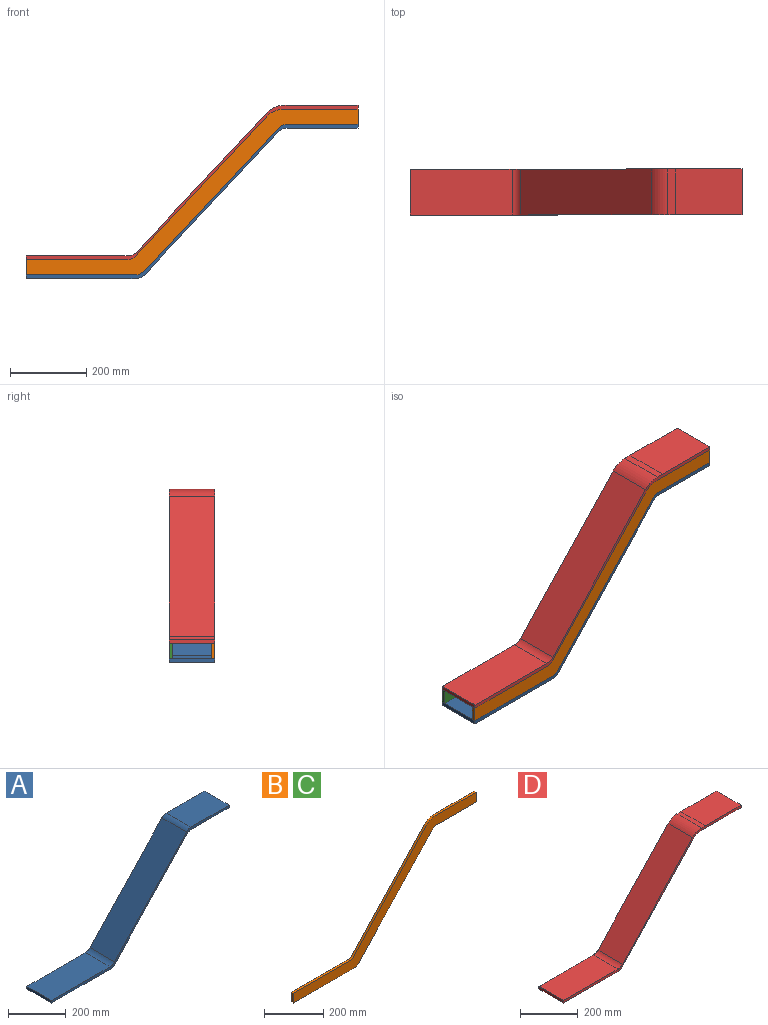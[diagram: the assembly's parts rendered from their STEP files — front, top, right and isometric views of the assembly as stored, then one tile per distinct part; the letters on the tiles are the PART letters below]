
ASSEMBLY  parts=4 mates=5
PART A: 15 faces, bbox 869.5x120x403.8 mm
  f0: cylinder r=30mm len=120mm, axis (0,1,0), area 2942mm2, adj f1,f12,f13,f14
  f1: plane 185.87x120mm, normal (0,0,-1), area 22305mm2, adj f0,f2,f13,f14
  f2: plane 120x9.99mm, normal (1,0,0), area 1198.4mm2, adj f1,f3,f13,f14
  f3: plane 187.01x120mm, normal (0,0,1), area 22441.2mm2, adj f2,f4,f13,f14
  f4: cylinder r=30mm len=120mm, axis (0,1,0), area 2942mm2, adj f3,f5,f13,f14
  f5: plane 374.85x351.71mm, normal (-0.73,0,0.68), area 61682.5mm2, adj f4,f6,f13,f14
  f6: cylinder r=30mm len=120mm, axis (0,1,0), area 2942mm2, adj f5,f7,f13,f14
  f7: plane 287.01x120mm, normal (0,0,1), area 34441.2mm2, adj f6,f8,f13,f14
  f8: plane 120x10mm, normal (-1,0,0), area 1200mm2, adj f7,f9,f13,f14
  f9: plane 120x1.14mm, normal (0.01,0,-1), area 136.3mm2, adj f8,f10,f13,f14
  f10: plane 287.01x120mm, normal (0,0,-1), area 34441.2mm2, adj f9,f11,f13,f14
  f11: cylinder r=30mm len=120mm, axis (0,1,0), area 2942mm2, adj f10,f12,f13,f14
  f12: plane 374.85x351.71mm, normal (0.73,0,-0.68), area 61682.5mm2, adj f0,f11,f13,f14
  f13: plane 869.49x403.8mm, normal (0,-1,0), area 9130.4mm2, adj f0,f1,f2,f3,f4,f5,f6,f7
  f14: plane 869.49x403.8mm, normal (0,1,0), area 9130.4mm2, adj f0,f1,f2,f3,f4,f5,f6,f7
PART B: 14 faces, bbox 869.5x9x433.8 mm
  f0: plane 40x9mm, normal (1,0,0), area 360mm2, adj f1,f11,f12,f13
  f1: plane 194.64x9mm, normal (0,0,1), area 1751.7mm2, adj f0,f2,f12,f13
  f2: cylinder r=60mm len=43.76mm, axis (0,1,0), area 441.3mm2, adj f1,f3,f12,f13
  f3: plane 365.38x342.83mm, normal (-0.73,0,0.68), area 4509.3mm2, adj f2,f4,f12,f13
  f4: cylinder r=30mm len=21.88mm, axis (0,1,0), area 220.7mm2, adj f3,f5,f12,f13
  f5: plane 266.39x9mm, normal (0,0,1), area 2397.6mm2, adj f4,f6,f12,f13
  f6: plane 40x9mm, normal (-1,0,0), area 360mm2, adj f5,f7,f12,f13
  f7: plane 287.01x9mm, normal (0,0,-1), area 2583.1mm2, adj f6,f8,f12,f13
  f8: cylinder r=30mm len=21.88mm, axis (0,1,0), area 220.7mm2, adj f7,f9,f12,f13
  f9: plane 374.85x351.71mm, normal (0.73,0,-0.68), area 4626.2mm2, adj f8,f10,f12,f13
  f10: cylinder r=30mm len=21.88mm, axis (0,1,0), area 220.7mm2, adj f9,f11,f12,f13
  f11: plane 187.01x9mm, normal (0,0,-1), area 1683.1mm2, adj f0,f10,f12,f13
  f12: plane 869.49x433.8mm, normal (0,-1,0), area 42832.1mm2, adj f0,f1,f2,f3,f4,f5,f6,f7
  f13: plane 869.49x433.8mm, normal (0,1,0), area 42832.1mm2, adj f0,f1,f2,f3,f4,f5,f6,f7
PART C: same geometry as B
PART D: 16 faces, bbox 869.5x120x403.8 mm
  f0: plane 175.2x120mm, normal (0,0,1), area 21024.1mm2, adj f1,f13,f14,f15
  f1: plane 120x18.65mm, normal (0,0,1), area 2237.9mm2, adj f0,f2,f14,f15
  f2: cylinder r=60mm len=120mm, axis (0,1,0), area 5884.1mm2, adj f1,f3,f14,f15
  f3: plane 365.38x342.83mm, normal (-0.73,0,0.68), area 60123.7mm2, adj f2,f4,f14,f15
  f4: cylinder r=30mm len=120mm, axis (0,1,0), area 2942mm2, adj f3,f5,f14,f15
  f5: plane 266.39x120mm, normal (0,0,1), area 31967.4mm2, adj f4,f6,f14,f15
  f6: plane 120x0.79mm, normal (0.05,0,1), area 94.5mm2, adj f5,f7,f14,f15
  f7: plane 120x10mm, normal (-1,0,0), area 1200mm2, adj f6,f8,f14,f15
  f8: plane 266.39x120mm, normal (0,0,-1), area 31967.4mm2, adj f7,f9,f14,f15
  f9: cylinder r=30mm len=120mm, axis (0,1,0), area 2942mm2, adj f8,f10,f14,f15
  f10: plane 365.38x342.83mm, normal (0.73,0,-0.68), area 60123.7mm2, adj f9,f11,f14,f15
  f11: cylinder r=60mm len=120mm, axis (0,1,0), area 5884.1mm2, adj f10,f12,f14,f15
  f12: plane 194.64x120mm, normal (0,0,-1), area 23356.3mm2, adj f11,f13,f14,f15
  f13: plane 120x10mm, normal (1,0,0), area 1200mm2, adj f0,f12,f14,f15
  f14: plane 869.49x403.8mm, normal (0,-1,0), area 8356.4mm2, adj f0,f1,f2,f3,f4,f5,f6,f7
  f15: plane 869.49x403.8mm, normal (0,1,0), area 8356.4mm2, adj f0,f1,f2,f3,f4,f5,f6,f7
PLACE A t=(-90.74,300.49,-216.41)mm fixed
PLACE B t=(-90.74,189.49,-216.41)mm
PLACE C t=(-90.74,300.49,-216.41)mm
PLACE D t=(-90.74,300.49,-216.41)mm
MATE planar C.f6 <-> A.f8  axis (-1,0,0) through (-90.74,295.99,-196.41)mm
MATE planar D.f8 <-> C.f5  axis (0,0,-1) through (42.45,240.49,-176.41)mm
MATE planar D.f15 <-> A.f14  axis (0,1,0) through (343.04,300.49,11.49)mm
MATE planar C.f7 <-> A.f7  axis (0,0,-1) through (-90.74,300.49,-216.41)mm
MATE planar C.f13 <-> A.f14  axis (0,1,0) through (-90.74,300.49,-196.41)mm
